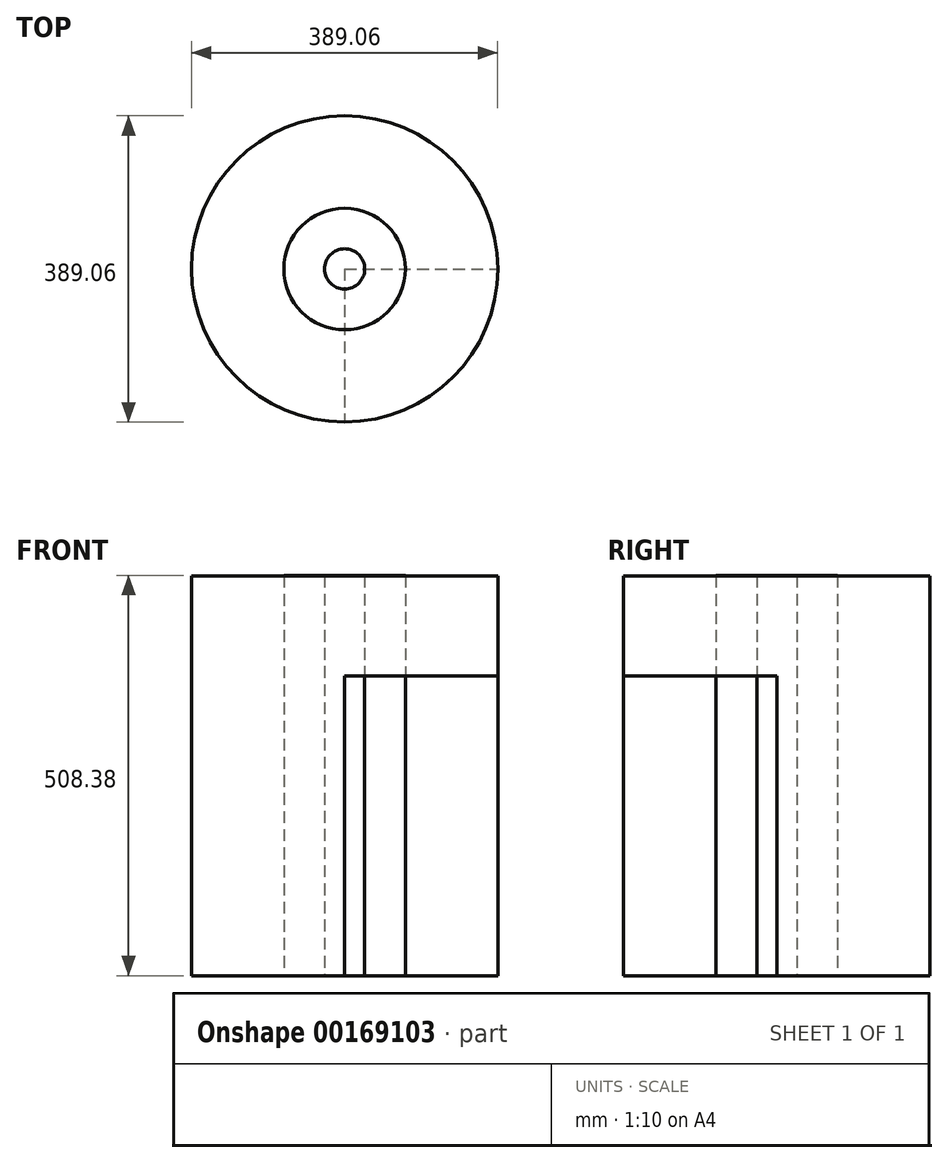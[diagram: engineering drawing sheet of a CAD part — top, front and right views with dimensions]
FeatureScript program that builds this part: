
annotation { "Feature Type Name" : "Feature", "Feature Type Description" : "" }
export const myFeature = defineFeature(function(context is Context, id is Id, definition is map)
    precondition{}
    {
        {
            var Q0;
            Q0=qCreatedBy(makeId("Top.planeOp"),FACE);
            var sketch = newSketch(context, id + "F0", { "sketchPlane" : qUnion([Q0])});
            skCircle(sketch, "E0", {"center": v(0, 0) * mm, "radius": 194.53 * mm});
            skSolve(sketch);
        }
        {
            var Q0;
            Q0=qCreatedBy(makeId("Top.planeOp"),FACE);
            var sketch = newSketch(context, id + "F1", { "sketchPlane" : qUnion([Q0])});
            skCircle(sketch, "E1", {"center": v(0, 0) * mm, "radius": 77.21 * mm});
            skSolve(sketch);
        }
        {
            var Q0;
            Q0=qCreatedBy(makeId("Top.planeOp"),FACE);
            var sketch = newSketch(context, id + "F2", { "sketchPlane" : qUnion([Q0])});
            skCircle(sketch, "E2", {"center": v(0, 0) * mm, "radius": 25.53 * mm});
            skSolve(sketch);
        }
        {
            var Q0;
            Q0=makeQuery(id+"F0.imprint","IMPRINT",FACE,{"disambiguationData":[TD([[makeQuery(id+"F0.imprint","IMPRINT",EDGE,{"derivedFrom":sQuery(id+"F0.wireOp",EDGE,"E0")}),1.0]])]});
            extrude(context, id + "F3", {"entities" : qUnion([Q0]), "depth" : 508 * mm});
        }
        {
            var Q0;
            Q0=makeQuery(id+"F1.imprint","IMPRINT",FACE,{"disambiguationData":[TD([[makeQuery(id+"F1.imprint","IMPRINT",EDGE,{"derivedFrom":sQuery(id+"F1.wireOp",EDGE,"E1")}),1.0]])]});
            extrude(context, id + "F4", {"entities" : qUnion([Q0]), "depth" : 508.25 * mm});
        }
        {
            var Q0;
            Q0=makeQuery(id+"F2.imprint","IMPRINT",FACE,{"disambiguationData":[TD([[makeQuery(id+"F2.imprint","IMPRINT",EDGE,{"derivedFrom":sQuery(id+"F2.wireOp",EDGE,"E2")}),1.0]])]});
            extrude(context, id + "F5", {"entities" : qUnion([Q0]), "depth" : 508.38 * mm});
        }
        {
            var Q0;
            Q0=qCreatedBy(makeId("Top.planeOp"),FACE);
            var sketch = newSketch(context, id + "F6", { "sketchPlane" : qUnion([Q0])});
            skLineSegment(sketch, "E3", {"start": v(0, 0) * mm, "end": v(257.44, 0) * mm});
            skLineSegment(sketch, "E4", {"start": v(0, 0) * mm, "end": v(0, -271.83) * mm});
            skArc(sketch, "E5", {"start": v(257.44, 0) * mm, "mid": v(182.04, -182.04) * mm, "end": v(0, -257.44) * mm});
            skSolve(sketch);
        }
        {
            var Q0;
            {var subQ0=sQuery(id+"F6.wireOp",EDGE,"E3");Q0=makeQuery(id+"F6.imprint","IMPRINT",FACE,{"disambiguationData":[TD([[makeQuery(id+"F6.imprint","IMPRINT",EDGE,{"derivedFrom":subQ0}),-1.0]])]});}
            extrude(context, id + "F7", {"entities" : qUnion([Q0]), "operationType" : NewBodyOperationType.REMOVE, "depth" : 381 * mm});
        }
    });
